# Revit family: UTB2
name_source: partatom
category: Lighting Fixtures
revit_build: Autodesk Revit 2014 (Build: 20130308_1515(x64)
units: mm (PartAtom-declared; Revit-internal decimal feet)

## types (1)
- UTB2
    Apparent Load = 25 VA
    Bracket material = Paint - Hubbell -  Black
    Certificate = CSA certified to UL1598 for Damp Location and UL924
    Color Filter = 16777215
    Connector Description = Lighting Connector
    Default Elevation = 48 "
    Description = Utilibay™ High Bay
    Dimming Lamp Color Temperature Shift = <None>
    Emit Shape Visible in Rendering = No
    Emit from Circle Diameter = 12 "
    Features = Available in a high output version (24,000 lumens), a medium output version (18,000 lumens) and a low output version (12,000 lumens)
Efficacy up to 170 lm/W
NX Distributed Intelligence™ wired and wireless control capability available
Five reflector options to meet any lighting need
Three optional lenses to meet your shielding needs
Light weight construction for easy installation
Symmetrical design for consistent installed results
    Lamp = LED
    Load Classification = Lighting
    Manufacturer = Hubbell Industrial Lighting
    Model = UTB2
    More Photometric Link = https://www.hubbell.com
    Photometric Web File = UTB2-8-30- MH-WW-X-N-N-YY-CGS.ies
    Product Documentation Link = https://hubbellcdn.com
    Product Material = Paint - Hubbell - White Texture
    Product Page URL = https://www.hubbell.com
    Reflector Finish = Hubbell - White Glass
    Tilt Angle = -90.00°
    URL = http://www.hubbellindustrial.com
    Warranty = Five year warranty (Terms and Conditions Apply)
    Watt = 255 W
    Wattage Comments = 255 W/ 167 W

## geometry (parser evidence)
native form markers: Blend x2, Sweep x4
no freeform markers — native parametric forms only
